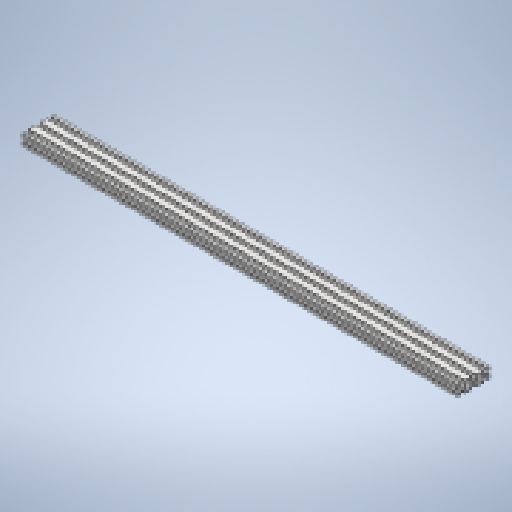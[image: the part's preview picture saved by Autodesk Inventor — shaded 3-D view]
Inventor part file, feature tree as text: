
AUTODESK INVENTOR PART (.ipt)
format: ipt  version: 2023 (Build 270158000, 158)  size: 461,824 bytes
history: native  units: mm
features: mirror x5, extrude x2, sketch x2
ambient origin geometry x8: Origin, YZ Plane, XZ Plane, XY Plane, X Axis, Y Axis, Z Axis, Center Point
bodies: Solid1 (feature_tree)
feature tree (9):
  extrude  "Extrusion1"  Depth=10.0mm
  mirror  "Mirror1"
  mirror  "Mirror2"
  mirror  "Mirror3"
  extrude  "Extrusion2"  Depth=0.5mm
  mirror  "Mirror4"
  mirror  "Mirror5"
  sketch  "Sketch1"  dims[d1=0.5mm d2=10.0mm]
  sketch  "Sketch2"  dims[d3=5.5mm d4=3.7mm d5=2.5mm d8=10.0mm d9=1.5mm d11=6.2mm d12=135.0deg d13=1.5mm d14=800.0mm d15=0.0mm d16=135.0deg d17=90.0deg d18=0.5mm d19=0.5mm d20=1.0mm d21=1.5mm d22=10.0mm d23=11.0mm d24=7.4mm d25=6.4mm d26=10.0mm d27=800.0mm d28=0.0mm d29=0.5mm d30=0.872665mm d31=0.5mm d32=0.872665mm]
